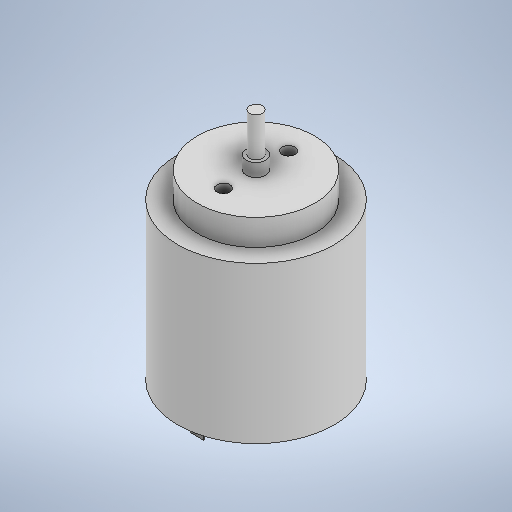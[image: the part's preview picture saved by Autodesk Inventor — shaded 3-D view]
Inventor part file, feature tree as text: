
AUTODESK INVENTOR PART (.ipt)
format: ipt  version: 2025.2 (Build 292293000, 293)  size: 282,624 bytes
history: native  units: mm
features: sketch x9, extrude x8
ambient origin geometry x8: Origin, YZ Plane, XZ Plane, XY Plane, X Axis, Y Axis, Z Axis, Center Point
bodies: Solid1 (feature_tree)
feature tree (17):
  extrude  "Extrusion1"  Depth=24.0mm TaperAngle=0.0deg
  extrude  "Extrusion2"  Depth=4.0mm TaperAngle=0.0deg
  extrude  "Extrusion3"  Depth=3.0mm
  extrude  "Extrusion4"  Depth=8.0mm TaperAngle=0.0deg
  extrude  "Extrusion5"  Depth=2.0mm
  extrude  "Extrusion6"  Depth=4.0mm
  extrude  "Extrusion7"  Depth=2.0mm
  extrude  "Extrusion8"  Depth=2.0mm
  sketch  "Sketch9"  dims[d23=2.0mm d24=2.0mm d25=0.0mm]
  sketch  "Sketch1"  dims[d0=24.0mm d1=24.0mm d2=0.0mm]
  sketch  "Sketch2"  dims[d3=18.0mm d4=4.0mm d5=0.0mm]
  sketch  "Sketch3"  dims[d6=2.0mm d7=3.0mm]
  sketch  "Sketch4"  dims[d8=2.0mm d9=0.0mm d10=8.0mm d11=0.0mm]
  sketch  "Sketch5"  dims[d12=2.0mm d13=2.0mm]
  sketch  "Sketch6"  dims[d14=3.0mm d15=0.0mm d16=4.0mm]
  sketch  "Sketch7"  dims[d17=1.0mm d18=0.0mm d19=2.0mm]
  sketch  "Sketch8"  dims[d20=0.2mm d21=0.0mm d22=2.0mm]
